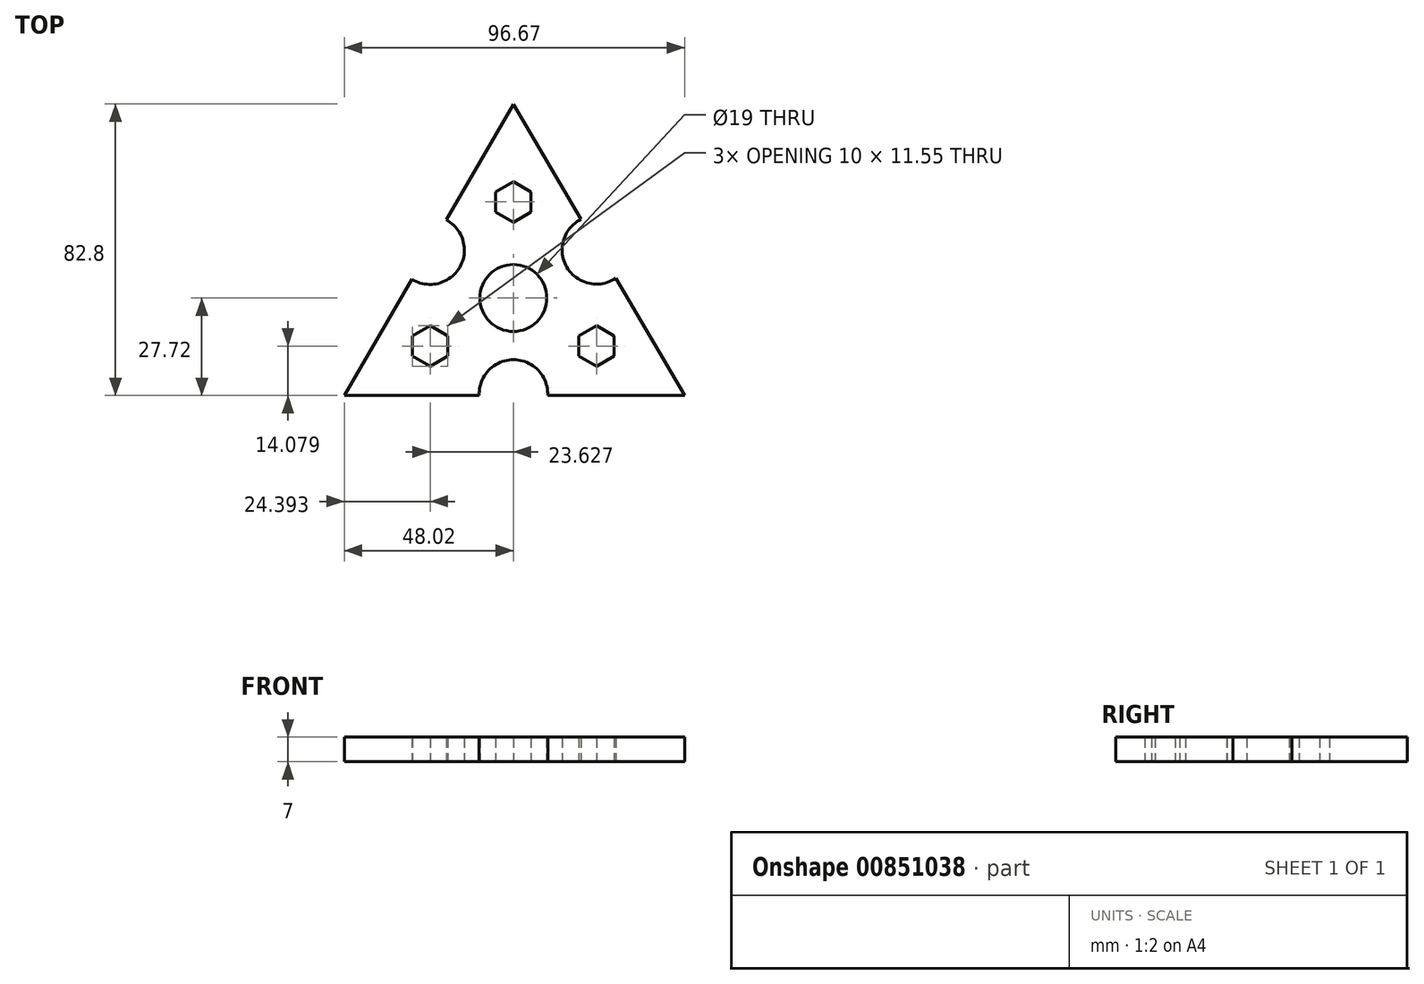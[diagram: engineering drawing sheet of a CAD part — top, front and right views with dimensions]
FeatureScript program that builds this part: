
annotation { "Feature Type Name" : "Feature", "Feature Type Description" : "" }
export const myFeature = defineFeature(function(context is Context, id is Id, definition is map)
    precondition{}
    {
        {
            var Q0;
            Q0=qCreatedBy(makeId("Top.planeOp"),FACE);
            var sketch = newSketch(context, id + "F0", { "sketchPlane" : qUnion([Q0])});
            skCircle(sketch, "E0", {"center": v(0, 0) * mm, "radius": 9.5 * mm});
            skPoint(sketch, "E1.center.orphan", {"position": v(-23.65, 13.6) * mm});
            skPoint(sketch, "E2.1.1.start.orphan", {"position": v(-35.82, -7.48) * mm});
            skPoint(sketch, "E3.end.orphan", {"position": v(-11.48, 34.69) * mm});
            skLineSegment(sketch, "E4", {"start": v(0, 55.08) * mm, "end": v(-19.07, 22.2) * mm});
            skLineSegment(sketch, "E5", {"start": v(-48.02, -27.72) * mm, "end": v(-9.69, -27.72) * mm});
            skLineSegment(sketch, "E6", {"start": v(48.65, -27.72) * mm, "end": v(29.07, 5.61) * mm});
            skArc(sketch, "E7", {"start": v(-28.84, 5.35) * mm, "mid": v(-15.22, 8.71) * mm, "end": v(-19.07, 22.2) * mm});
            skArc(sketch, "E8.1.0", {"start": v(9.78, -27.72) * mm, "mid": v(0.04, -17.54) * mm, "end": v(-9.69, -27.72) * mm});
            skArc(sketch, "E8.2.0", {"start": v(19.22, 22.38) * mm, "mid": v(15.2, 8.74) * mm, "end": v(29.07, 5.61) * mm});
            skLineSegment(sketch, "E9.trimOffspring", {"start": v(-28.84, 5.35) * mm, "end": v(-48.02, -27.72) * mm});
            skLineSegment(sketch, "E10.trimOffspring", {"start": v(19.22, 22.38) * mm, "end": v(0, 55.08) * mm});
            skLineSegment(sketch, "E11.trimOffspring", {"start": v(9.78, -27.72) * mm, "end": v(48.65, -27.72) * mm});
            skCircle(sketch, "E12", {"center": v(0, 0) * mm, "radius": 27.28 * mm, "construction": true});
            skPoint(sketch, "E13", {"position": v(0, 27.28) * mm});
            skLineSegment(sketch, "E14.0", {"start": v(0, 27.28) * mm, "end": v(23.63, -13.64) * mm, "construction": true});
            skLineSegment(sketch, "E14.1", {"start": v(23.63, -13.64) * mm, "end": v(-23.63, -13.64) * mm, "construction": true});
            skLineSegment(sketch, "E14.2", {"start": v(-23.63, -13.64) * mm, "end": v(0, 27.28) * mm, "construction": true});
            skCircle(sketch, "E15.cCircle", {"center": v(0, 27.28) * mm, "radius": 5.77 * mm, "construction": true});
            skLineSegment(sketch, "E15.0", {"start": v(0, 33.06) * mm, "end": v(5, 30.17) * mm});
            skLineSegment(sketch, "E15.1", {"start": v(5, 30.17) * mm, "end": v(5, 24.4) * mm});
            skLineSegment(sketch, "E15.2", {"start": v(5, 24.4) * mm, "end": v(0, 21.5) * mm});
            skLineSegment(sketch, "E15.3", {"start": v(0, 21.5) * mm, "end": v(-5, 24.4) * mm});
            skLineSegment(sketch, "E15.4", {"start": v(-5, 24.4) * mm, "end": v(-5, 30.17) * mm});
            skLineSegment(sketch, "E15.5", {"start": v(-5, 30.17) * mm, "end": v(0, 33.06) * mm});
            skLineSegment(sketch, "E16", {"start": v(0, 0) * mm, "end": v(48.65, -27.72) * mm, "construction": true});
            skLineSegment(sketch, "E17", {"start": v(0, 0) * mm, "end": v(-48.02, -27.72) * mm, "construction": true});
            skLineSegment(sketch, "E18.1.0", {"start": v(-28.63, -16.53) * mm, "end": v(-28.63, -10.75) * mm});
            skLineSegment(sketch, "E18.1.1", {"start": v(-28.63, -10.75) * mm, "end": v(-23.63, -7.87) * mm});
            skLineSegment(sketch, "E18.1.2", {"start": v(-23.63, -7.87) * mm, "end": v(-18.63, -10.75) * mm});
            skLineSegment(sketch, "E18.1.3", {"start": v(-18.63, -10.75) * mm, "end": v(-18.63, -16.53) * mm});
            skLineSegment(sketch, "E18.1.4", {"start": v(-18.63, -16.53) * mm, "end": v(-23.63, -19.41) * mm});
            skLineSegment(sketch, "E18.1.5", {"start": v(-23.63, -19.41) * mm, "end": v(-28.63, -16.53) * mm});
            skLineSegment(sketch, "E18.2.0", {"start": v(28.63, -16.53) * mm, "end": v(23.63, -19.41) * mm});
            skLineSegment(sketch, "E18.2.1", {"start": v(23.63, -19.41) * mm, "end": v(18.63, -16.53) * mm});
            skLineSegment(sketch, "E18.2.2", {"start": v(18.63, -16.53) * mm, "end": v(18.63, -10.75) * mm});
            skLineSegment(sketch, "E18.2.3", {"start": v(18.63, -10.75) * mm, "end": v(23.63, -7.87) * mm});
            skLineSegment(sketch, "E18.2.4", {"start": v(23.63, -7.87) * mm, "end": v(28.63, -10.75) * mm});
            skLineSegment(sketch, "E18.2.5", {"start": v(28.63, -10.75) * mm, "end": v(28.63, -16.53) * mm});
            skSolve(sketch);
        }
        {
            var Q0;
            Q0=makeQuery(id+"F0.imprint","IMPRINT",FACE,{"disambiguationData":[TD([[makeQuery(id+"F0.imprint","IMPRINT",EDGE,{"derivedFrom":sQuery(id+"F0.wireOp",EDGE,"E0")}),-1.0]])]});
            extrude(context, id + "F1", {"entities" : qUnion([Q0]), "depth" : 7 * mm, "offsetDistance" : 25 * mm});
        }
    });
